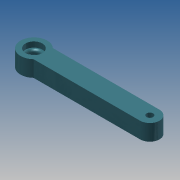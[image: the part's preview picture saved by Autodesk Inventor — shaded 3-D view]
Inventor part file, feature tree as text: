
AUTODESK INVENTOR PART (.ipt)
format: ipt  version: 2013 (Build 170138000, 138)  size: 129,024 bytes
history: native  units: mm
features: extrude x5, sketch x5, fillet x2
ambient origin geometry x8: Origin, YZ Plane, XZ Plane, XY Plane, X Axis, Y Axis, Z Axis, Center Point
bodies: Solid1 (feature_tree)
feature tree (12):
  extrude  "Extrusion1"  Depth=12.6mm
  extrude  "Extrusion2"  Depth=8.5mm
  extrude  "Extrusion5"  Depth=22.0mm
  extrude  "Extrusion6"  Depth=35.0mm
  extrude  "Extrusion7"  Depth=7.0mm TaperAngle=0.0deg
  fillet  "Fillet1"  Radius=13.0mm
  fillet  "Fillet2"  Radius=8.0mm
  sketch  "Sketch1"  dims[d0=151.5mm d2=12.6mm]
  sketch  "Sketch2"  dims[d3=15.0mm d4=8.5mm]
  sketch  "Sketch6"  dims[d5=21.1mm d6=0.0mm d7=22.0mm]
  sketch  "Sketch7"  dims[d9=7.0mm d10=0.0mm d25=35.0mm]
  sketch  "Sketch8"  dims[d27=10.0mm d28=0.0mm d29=7.0mm d30=0.0mm d31=13.0mm d32=8.0mm d33=0.0mm d34=3.5mm d35=3.5mm]
